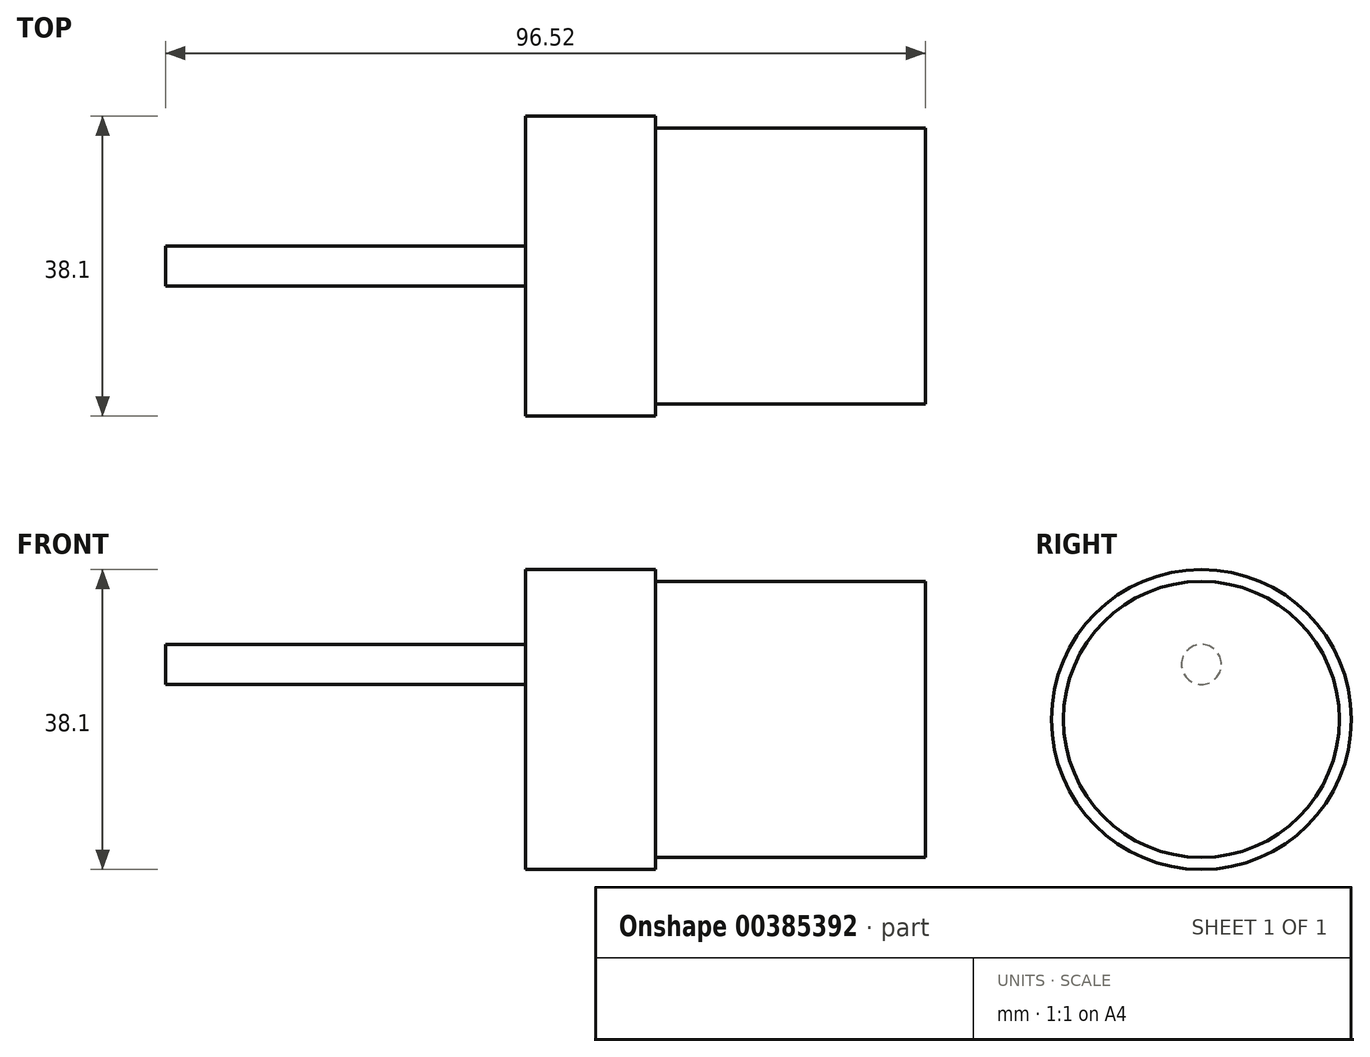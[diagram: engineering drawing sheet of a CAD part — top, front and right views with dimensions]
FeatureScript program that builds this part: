
annotation { "Feature Type Name" : "Feature", "Feature Type Description" : "" }
export const myFeature = defineFeature(function(context is Context, id is Id, definition is map)
    precondition{}
    {
        {
            var Q0;
            Q0=qCreatedBy(makeId("Front.planeOp"),FACE);
            var sketch = newSketch(context, id + "F0", { "sketchPlane" : qUnion([Q0])});
            skLineSegment(sketch, "E0", {"start": v(-4.8, 8.17) * mm, "end": v(11.71, 8.17) * mm});
            skLineSegment(sketch, "E1", {"start": v(11.71, 8.17) * mm, "end": v(11.71, 6.65) * mm});
            skLineSegment(sketch, "E2", {"start": v(11.71, 6.65) * mm, "end": v(46, 6.65) * mm});
            skLineSegment(sketch, "E3", {"start": v(46, 6.65) * mm, "end": v(46, -10.88) * mm});
            skLineSegment(sketch, "E4", {"start": v(46, -10.88) * mm, "end": v(-4.8, -10.88) * mm});
            skLineSegment(sketch, "E5", {"start": v(-4.8, -10.88) * mm, "end": v(-4.8, 8.17) * mm});
            skLineSegment(sketch, "E6", {"start": v(-4.8, -1.35) * mm, "end": v(-50.52, -1.35) * mm});
            skLineSegment(sketch, "E7", {"start": v(-50.52, -1.35) * mm, "end": v(-50.52, -3.9) * mm});
            skLineSegment(sketch, "E8", {"start": v(-50.52, -3.9) * mm, "end": v(-4.8, -3.9) * mm});
            skSolve(sketch);
        }
        {
            var Q0;
            {var subQ0=sQuery(id+"F0.wireOp",EDGE,"E0");Q0=makeQuery(id+"F0.imprint","IMPRINT",FACE,{"disambiguationData":[TD([[makeQuery(id+"F0.imprint","IMPRINT",EDGE,{"derivedFrom":subQ0}),-1.0]])]});}
            var Q1;
            Q1=sQuery(id+"F0.wireOp",EDGE,"E4");
            revolve(context, id + "F1", {"entities" : qUnion([Q0]), "axis" : qUnion([Q1]), "revolveType" : RevolveType.FULL});
        }
        {
            var Q0;
            {var subQ0=sQuery(id+"F0.wireOp",EDGE,"E6");Q0=makeQuery(id+"F0.imprint","IMPRINT",FACE,{"disambiguationData":[TD([[makeQuery(id+"F0.imprint","IMPRINT",EDGE,{"derivedFrom":subQ0}),1.0]])]});}
            var Q1;
            Q1=sQuery(id+"F0.wireOp",EDGE,"E8");
            revolve(context, id + "F2", {"operationType" : NewBodyOperationType.ADD, "entities" : qUnion([Q0]), "axis" : qUnion([Q1]), "revolveType" : RevolveType.FULL});
        }
    });
